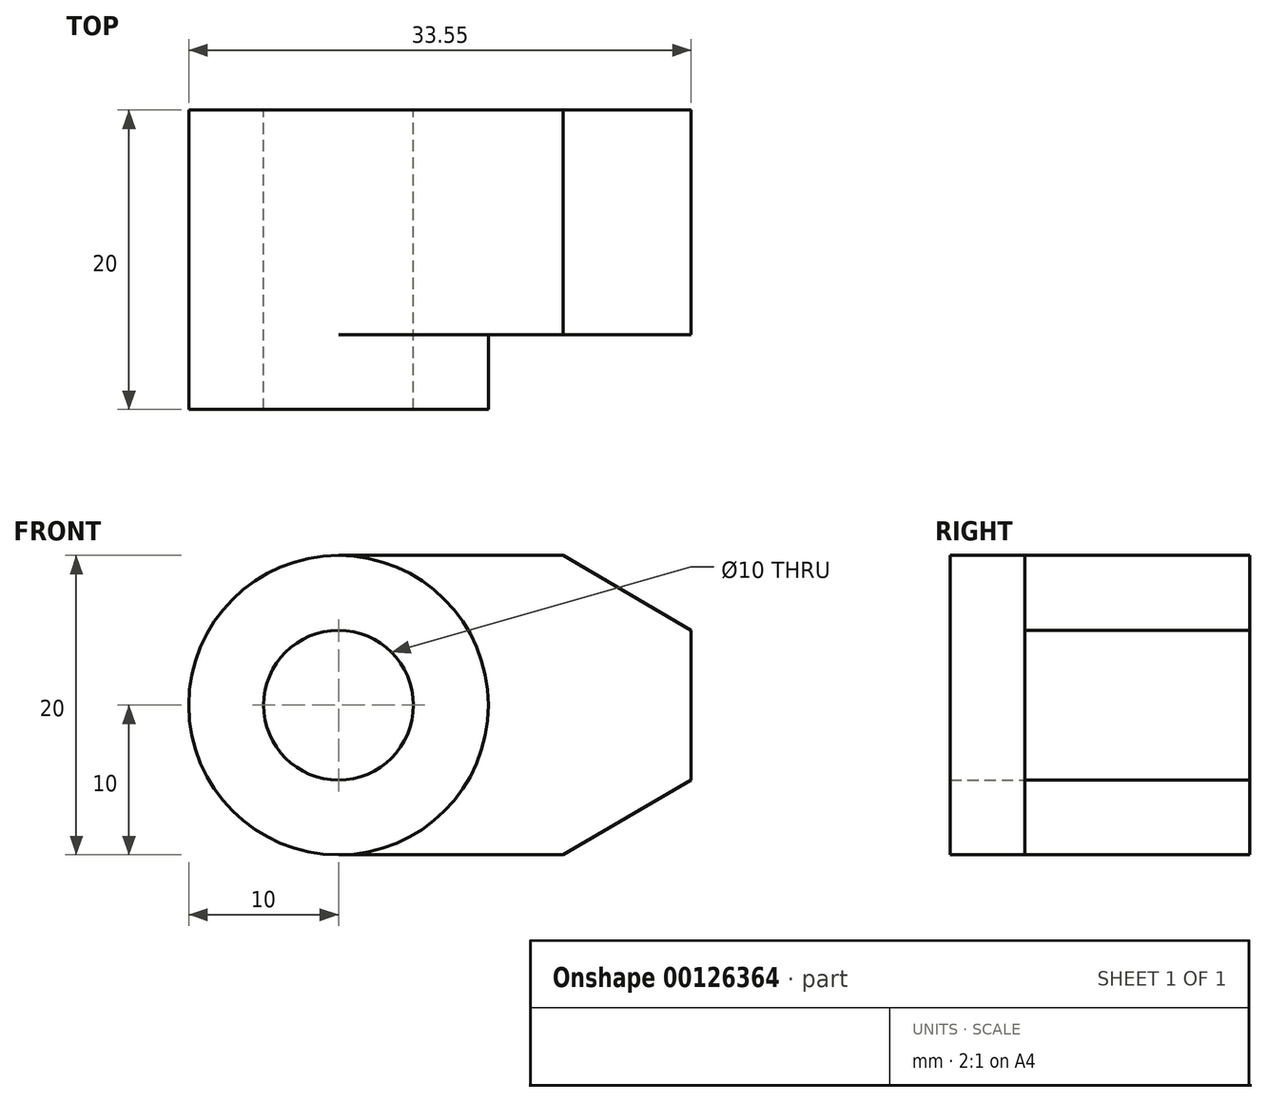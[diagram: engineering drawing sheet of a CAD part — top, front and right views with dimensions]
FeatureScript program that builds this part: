
annotation { "Feature Type Name" : "Feature", "Feature Type Description" : "" }
export const myFeature = defineFeature(function(context is Context, id is Id, definition is map)
    precondition{}
    {
        {
            var Q0;
            Q0=qCreatedBy(makeId("Front.planeOp"),FACE);
            var sketch = newSketch(context, id + "F0", { "sketchPlane" : qUnion([Q0])});
            skCircle(sketch, "E0", {"center": v(0, 0) * mm, "radius": 5 * mm});
            skCircle(sketch, "E1", {"center": v(0, 0) * mm, "radius": 10 * mm});
            skSolve(sketch);
        }
        {
            var Q0;
            Q0 = qSketchRegion(id + "F0", true);
            extrude(context, id + "F1", {"entities" : qUnion([Q0]), "depth" : 5 * mm});
        }
        {
            var Q0;
            Q0=qCreatedBy(makeId("Front.planeOp"),FACE);
            var sketch = newSketch(context, id + "F2", { "sketchPlane" : qUnion([Q0])});
            skCircle(sketch, "E2.0", {"center": v(0, 0) * mm, "radius": 10 * mm});
            skLineSegment(sketch, "E3", {"start": v(0, 10) * mm, "end": v(15, 10) * mm});
            skLineSegment(sketch, "E4", {"start": v(0, -10) * mm, "end": v(15, -10) * mm});
            skLineSegment(sketch, "E5", {"start": v(15, -10) * mm, "end": v(23.55, -5) * mm});
            skLineSegment(sketch, "E6", {"start": v(23.55, -5) * mm, "end": v(23.55, 5) * mm});
            skLineSegment(sketch, "E7", {"start": v(23.55, 5) * mm, "end": v(15, 10) * mm});
            skSolve(sketch);
        }
        {
            var Q0;
            Q0 = qSketchRegion(id + "F2", true);
            extrude(context, id + "F3", {"entities" : qUnion([Q0]), "operationType" : NewBodyOperationType.ADD, "oppositeDirection" : true, "depth" : 15 * mm});
        }
        {
            var Q0;
            Q0=qCreatedBy(makeId("Front.planeOp"),FACE);
            var sketch = newSketch(context, id + "F4", { "sketchPlane" : qUnion([Q0])});
            skCircle(sketch, "E8.0", {"center": v(0, 0) * mm, "radius": 5 * mm});
            skSolve(sketch);
        }
        {
            var Q0;
            Q0 = qSketchRegion(id + "F4", true);
            extrude(context, id + "F5", {"entities" : qUnion([Q0]), "operationType" : NewBodyOperationType.REMOVE, "endBound" : BoundingType.SYMMETRIC, "oppositeDirection" : true, "depth" : 49.82 * mm});
        }
    });
